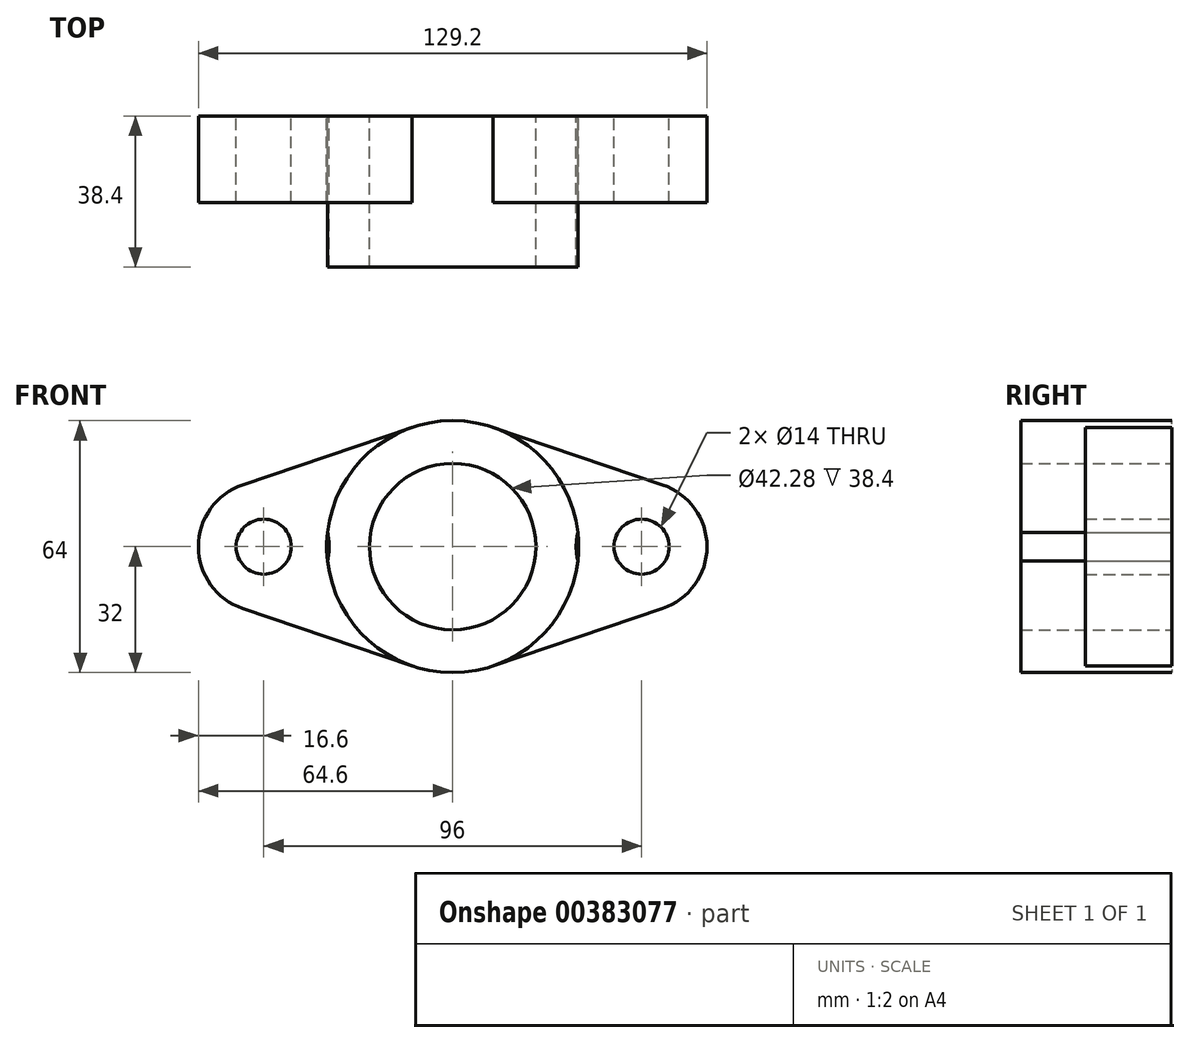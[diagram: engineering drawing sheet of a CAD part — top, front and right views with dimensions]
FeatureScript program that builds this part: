
annotation { "Feature Type Name" : "Feature", "Feature Type Description" : "" }
export const myFeature = defineFeature(function(context is Context, id is Id, definition is map)
    precondition{}
    {
        {
            var Q0;
            Q0=qCreatedBy(makeId("Front.planeOp"),FACE);
            var sketch = newSketch(context, id + "F0", { "sketchPlane" : qUnion([Q0])});
            skCircle(sketch, "E0", {"center": v(0, 0) * mm, "radius": 32 * mm});
            skCircle(sketch, "E1", {"center": v(-48, 0) * mm, "radius": 7 * mm});
            skCircle(sketch, "E2", {"center": v(48, 0) * mm, "radius": 7 * mm});
            skCircle(sketch, "E3", {"center": v(0, 0) * mm, "radius": 21.14 * mm});
            skCircle(sketch, "E4", {"center": v(48, 0) * mm, "radius": 16.6 * mm});
            skCircle(sketch, "E5", {"center": v(-48, 0) * mm, "radius": 16.6 * mm});
            skLineSegment(sketch, "E6", {"start": v(-10.26, 30.3) * mm, "end": v(-53.33, 15.73) * mm});
            skLineSegment(sketch, "E7", {"start": v(-53.33, -15.73) * mm, "end": v(-10.26, -30.3) * mm});
            skLineSegment(sketch, "E8", {"start": v(10.26, 30.3) * mm, "end": v(53.33, 15.73) * mm});
            skLineSegment(sketch, "E9", {"start": v(10.26, -30.3) * mm, "end": v(53.33, -15.73) * mm});
            skSolve(sketch);
        }
        {
            var Q0;
            {var subQ0=sQuery(id+"F0.wireOp",EDGE,"E7");Q0=makeQuery(id+"F0.imprint","IMPRINT",FACE,{"disambiguationData":[TD([[makeQuery(id+"F0.imprint","IMPRINT",EDGE,{"derivedFrom":subQ0}),1.0]])]});}
            var Q1;
            {var subQ0=sQuery(id+"F0.wireOp",EDGE,"E6");Q1=makeQuery(id+"F0.imprint","IMPRINT",FACE,{"disambiguationData":[TD([[makeQuery(id+"F0.imprint","IMPRINT",EDGE,{"derivedFrom":subQ0}),1.0]])]});}
            var Q2;
            {var subQ0=sQuery(id+"F0.wireOp",EDGE,"E8");Q2=makeQuery(id+"F0.imprint","IMPRINT",FACE,{"disambiguationData":[TD([[makeQuery(id+"F0.imprint","IMPRINT",EDGE,{"derivedFrom":subQ0}),-1.0]])]});}
            var Q3;
            Q3=makeQuery(id+"F0.imprint","IMPRINT",FACE,{"disambiguationData":[TD([[makeQuery(id+"F0.imprint","IMPRINT",EDGE,{"derivedFrom":sQuery(id+"F0.wireOp",EDGE,"E2")}),-1.0]])]});
            var Q4;
            {var subQ0=sQuery(id+"F0.wireOp",EDGE,"E9");Q4=makeQuery(id+"F0.imprint","IMPRINT",FACE,{"disambiguationData":[TD([[makeQuery(id+"F0.imprint","IMPRINT",EDGE,{"derivedFrom":subQ0}),1.0]])]});}
            var Q5;
            Q5=makeQuery(id+"F0.imprint","IMPRINT",FACE,{"disambiguationData":[TD([[makeQuery(id+"F0.imprint","IMPRINT",EDGE,{"derivedFrom":sQuery(id+"F0.wireOp",EDGE,"E1")}),-1.0]])]});
            extrude(context, id + "F1", {"entities" : qUnion([Q0, Q1, Q2, Q3, Q4, Q5]), "depth" : 22 * mm});
        }
        {
            var Q0;
            Q0=makeQuery(id+"F0.imprint","IMPRINT",FACE,{"disambiguationData":[TD([[makeQuery(id+"F0.imprint","IMPRINT",EDGE,{"derivedFrom":sQuery(id+"F0.wireOp",EDGE,"E3")}),-1.0]])]});
            extrude(context, id + "F2", {"entities" : qUnion([Q0]), "depth" : 38.4 * mm});
        }
    });
